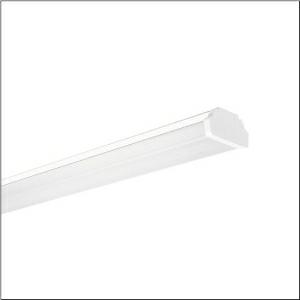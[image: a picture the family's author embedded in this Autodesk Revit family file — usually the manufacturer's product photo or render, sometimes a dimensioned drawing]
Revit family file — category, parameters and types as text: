
# Revit family: dus_r__31_mo_53bd81271v4080_fa57
name_source: partatom
category: Lighting Fixtures
units: mm (PartAtom-declared; Revit-internal decimal feet)

## family parameters
Cut with Voids When Loaded = No
Host = Face
Light Source = No
Part Type = Normal
Room Calculation Point = No
Round Connector Dimension = Use Diameter
Shared = No

## types (1)
- DUS® 31 MO (1 x LED, 7810 lm, 50.8 W, 4000K)
    Apparent Load = 51 VA
    CIE Flux Codes = 47 80 95 92 100
    Color Rendering = 80
    Color Temperature = 4000K
    Default Elevation = 1800 mm
    Description = DUS® 31 MOluminaire insert, length: 1.535mm, width: 81mm, height: 90mm, LED rated luminous flux: 7.810lm, light colour: 840, control gear: ON/OFF, control gear: ECG, with plug, 3-pole, with phase selection, mains connection: 220..240V, AC, 50/60Hz, primary optical cover: cover, of PMMA, light emission: direct distribution, primary light characteristic: symmetric, protection rating (complete): IP20, protection rating (LED compartment): IP50, insulation class (complete): insulation class I (protective earthing), certification: CE, ENEC, VDE, permissible ambient temperature for indoor applications: -35..+35°C, corresponds to IFS (International Featured Standards) requirements for safety and quality in the food industry, reducing of maximum allowable ambient temperature of 5°C with ceiling mounting, packaging unit: 1 piece
    Height = 95 mm
    Lamp = 1 x LED
    Lamp Light Flux = 7810 lm
    Lamp Power = 50.8 W
    Lamp count = 1
    Length = 1535 mm
    Luminous efficacy = 154 lm/W
    Manufacturer = Siteco
    ModVariant = No
    Model = 53BD81271V4080
    Mounting Place = Ceiling
    Mounting Type = Pendant
    Number of Poles = 1
    OnlyDefault = Yes
    Power Factor = 1
    Product Name = DUS® 31 MO
    Product group = luminaire insert
    ProductGroupID = 902
    Protection Class = Protection class I
    Protection Degree = IP 20
    RLX_Detail_Level = 1
    RlxData = <blob elided: 38345 chars, md5=256f9ff8>
    Socket = socket
    Standby Power = 0 W
    System Light Flux = 7810 lm
    System Power = 51 W
    Type Comments = Product without accessories
    Type Image = l_1003451.jpg
    URL = http://relux.com
    VarID = ---
    Voltage = 0 V
    Weight = 0.00 kg
    Width = 81 mm

## geometry (parser evidence)
native form markers: Blend x4, Sweep x13
no freeform markers — native parametric forms only
